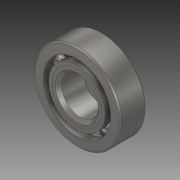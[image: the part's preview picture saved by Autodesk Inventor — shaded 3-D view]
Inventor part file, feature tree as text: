
AUTODESK INVENTOR PART (.ipt)
format: ipt  version: 2020 (Build 240168000, 168)  size: 594,432 bytes
history: native  units: in
note: dims shown in document units (in); Inventor stores cm internally (conversion verified against a paired STEP export)
features: other x9, revolve x4
ambient origin geometry x8: Origin, YZ Plane, XZ Plane, XY Plane, X Axis, Y Axis, Z Axis, Center Point
bodies: Solid1 (feature_tree), Solid2 (feature_tree), Solid3 (feature_tree), Solid4 (feature_tree), Solid5 (feature_tree), Solid6 (feature_tree), Solid7 (feature_tree), Solid8 (feature_tree), Solid9 (feature_tree), Solid10 (feature_tree), Solid11 (feature_tree), Solid12 (feature_tree), Solid13 (feature_tree)
feature tree (13):
  revolve  "Revolve1"  [1 undecoded]
  revolve  "Revolve2"  [1 undecoded]
  revolve  "Revolve3"  [1 undecoded]
  revolve  "Revolve4"  [1 undecoded]
  other  "CirPattern1[1]"
  other  "CirPattern1[2]"
  other  "CirPattern1[3]"
  other  "CirPattern1[4]"
  other  "CirPattern1[5]"
  other  "CirPattern1[6]"
  other  "CirPattern1[7]"
  other  "CirPattern1[8]"
  other  "CirPattern1[9]"
note: 4 required parameter values undecoded (feature->parameter linkage not recoverable at this tier; creation-order binding heuristic only, values carry confidence <= 0.55)
